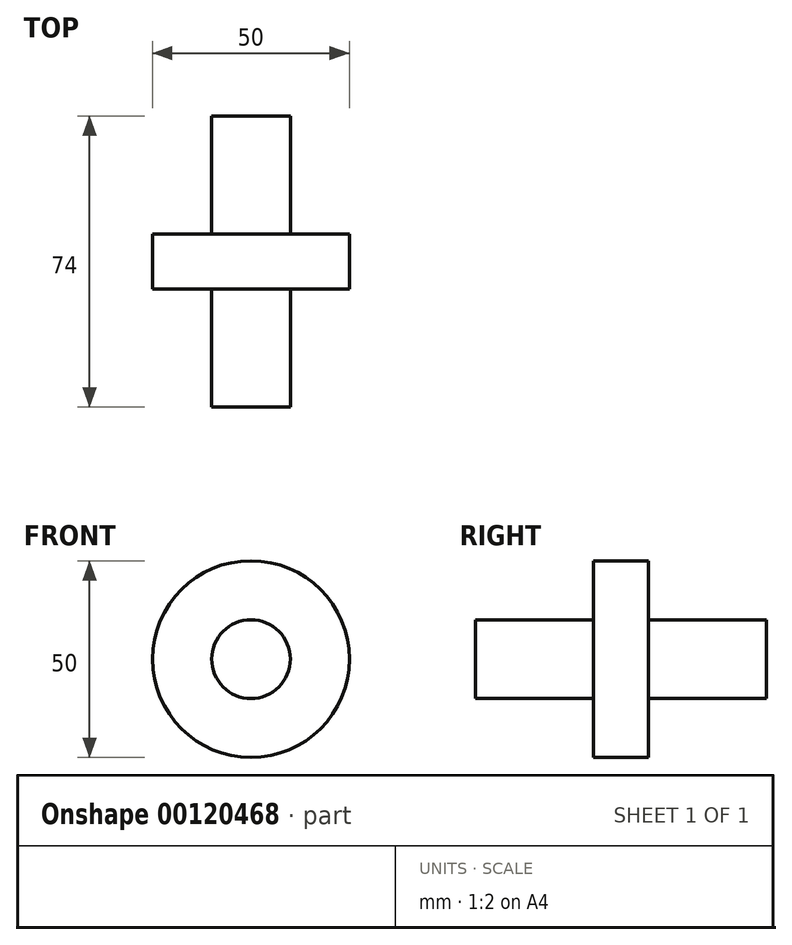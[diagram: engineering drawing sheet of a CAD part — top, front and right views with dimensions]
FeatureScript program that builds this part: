
annotation { "Feature Type Name" : "Feature", "Feature Type Description" : "" }
export const myFeature = defineFeature(function(context is Context, id is Id, definition is map)
    precondition{}
    {
        {
            var Q0;
            Q0=qCreatedBy(makeId("Top.planeOp"),FACE);
            var sketch = newSketch(context, id + "F0", { "sketchPlane" : qUnion([Q0])});
            skLineSegment(sketch, "E0", {"start": v(0, 41.62) * mm, "end": v(0, -32.38) * mm});
            skLineSegment(sketch, "E1", {"start": v(0, -32.38) * mm, "end": v(10, -32.38) * mm});
            skLineSegment(sketch, "E2", {"start": v(10, -32.38) * mm, "end": v(10, -2.38) * mm});
            skLineSegment(sketch, "E3", {"start": v(10, -2.38) * mm, "end": v(25, -2.38) * mm});
            skLineSegment(sketch, "E4", {"start": v(25, -2.38) * mm, "end": v(25, 11.62) * mm});
            skLineSegment(sketch, "E5", {"start": v(25, 11.62) * mm, "end": v(10, 11.62) * mm});
            skLineSegment(sketch, "E6", {"start": v(10, 11.62) * mm, "end": v(10, 41.62) * mm});
            skLineSegment(sketch, "E7", {"start": v(0, 41.62) * mm, "end": v(10, 41.62) * mm});
            skSolve(sketch);
        }
        {
            var Q0;
            Q0=makeQuery(id+"F0.imprint","IMPRINT",FACE,{"disambiguationData":[TD([[makeQuery(id+"F0.imprint","IMPRINT",EDGE,{"derivedFrom":sQuery(id+"F0.wireOp",EDGE,"E0")}),1.0]])]});
            var Q1;
            Q1=sQuery(id+"F0.wireOp",EDGE,"E0");
            revolve(context, id + "F1", {"entities" : qUnion([Q0]), "axis" : qUnion([Q1]), "revolveType" : RevolveType.FULL});
        }
    });
